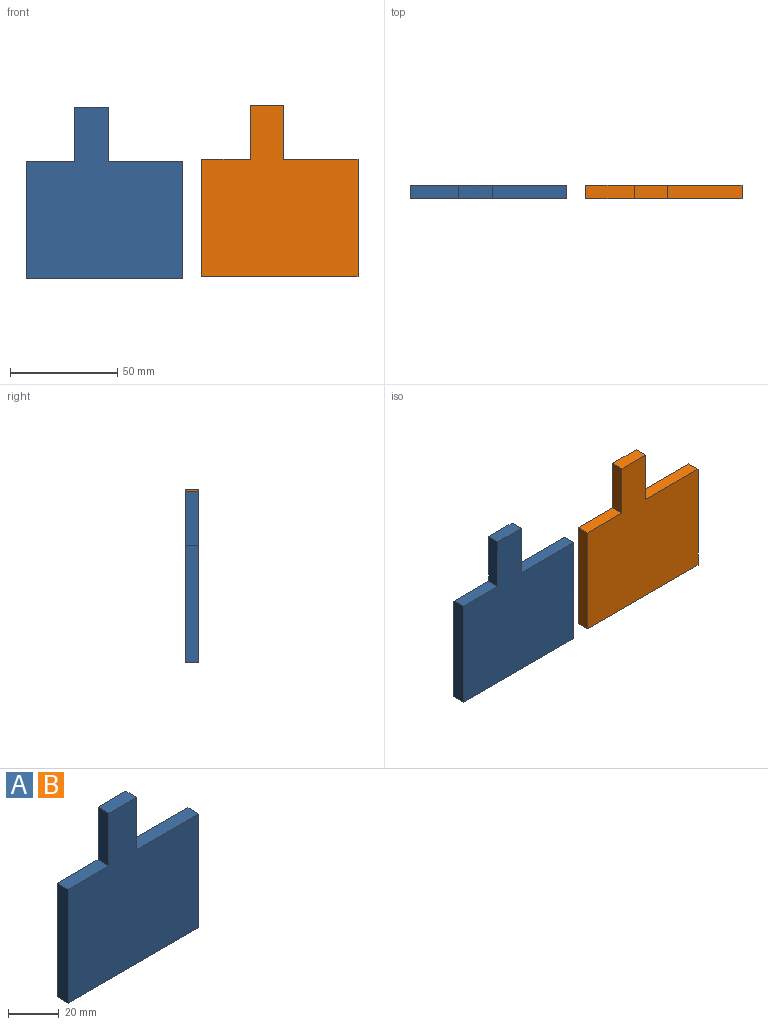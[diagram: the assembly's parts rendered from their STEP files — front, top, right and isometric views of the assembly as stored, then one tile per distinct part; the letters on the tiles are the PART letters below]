
ASSEMBLY  parts=2 mates=1
PART A: 10 faces, bbox 72.9x6.1x80.2 mm
  f0: plane 34.66x6.1mm, normal (0,0,1), area 211.3mm2, adj f4,f5,f6,f8
  f1: plane 22.8x6.1mm, normal (0,0,1), area 139mm2, adj f2,f5,f6,f7
  f2: plane 54.8x6.1mm, normal (-1,0,0), area 334.1mm2, adj f1,f3,f5,f6
  f3: plane 72.94x6.1mm, normal (0,0,-1), area 444.7mm2, adj f2,f4,f5,f6
  f4: plane 54.8x6.1mm, normal (1,0,0), area 334.1mm2, adj f0,f3,f5,f6
  f5: plane 80.2x72.94mm, normal (0,-1,0), area 4390.9mm2, adj f0,f1,f2,f3,f4,f7,f8,f9
  f6: plane 80.2x72.94mm, normal (0,1,0), area 4390.9mm2, adj f0,f1,f2,f3,f4,f7,f8,f9
  f7: plane 25.4x6.1mm, normal (-1,0,0), area 154.8mm2, adj f1,f5,f6,f9
  f8: plane 25.4x6.1mm, normal (1,0,0), area 154.8mm2, adj f0,f5,f6,f9
  f9: plane 15.48x6.1mm, normal (0,0,1), area 94.4mm2, adj f5,f6,f7,f8
PART B: same geometry as A
PLACE A t=(-58.01,-0.44,3.96)mm
PLACE B t=(23.89,-0.44,4.9)mm
MATE planar B.f5 <-> A.f5  axis (0,-1,0) through (21.54,-6.53,8.68)mm
